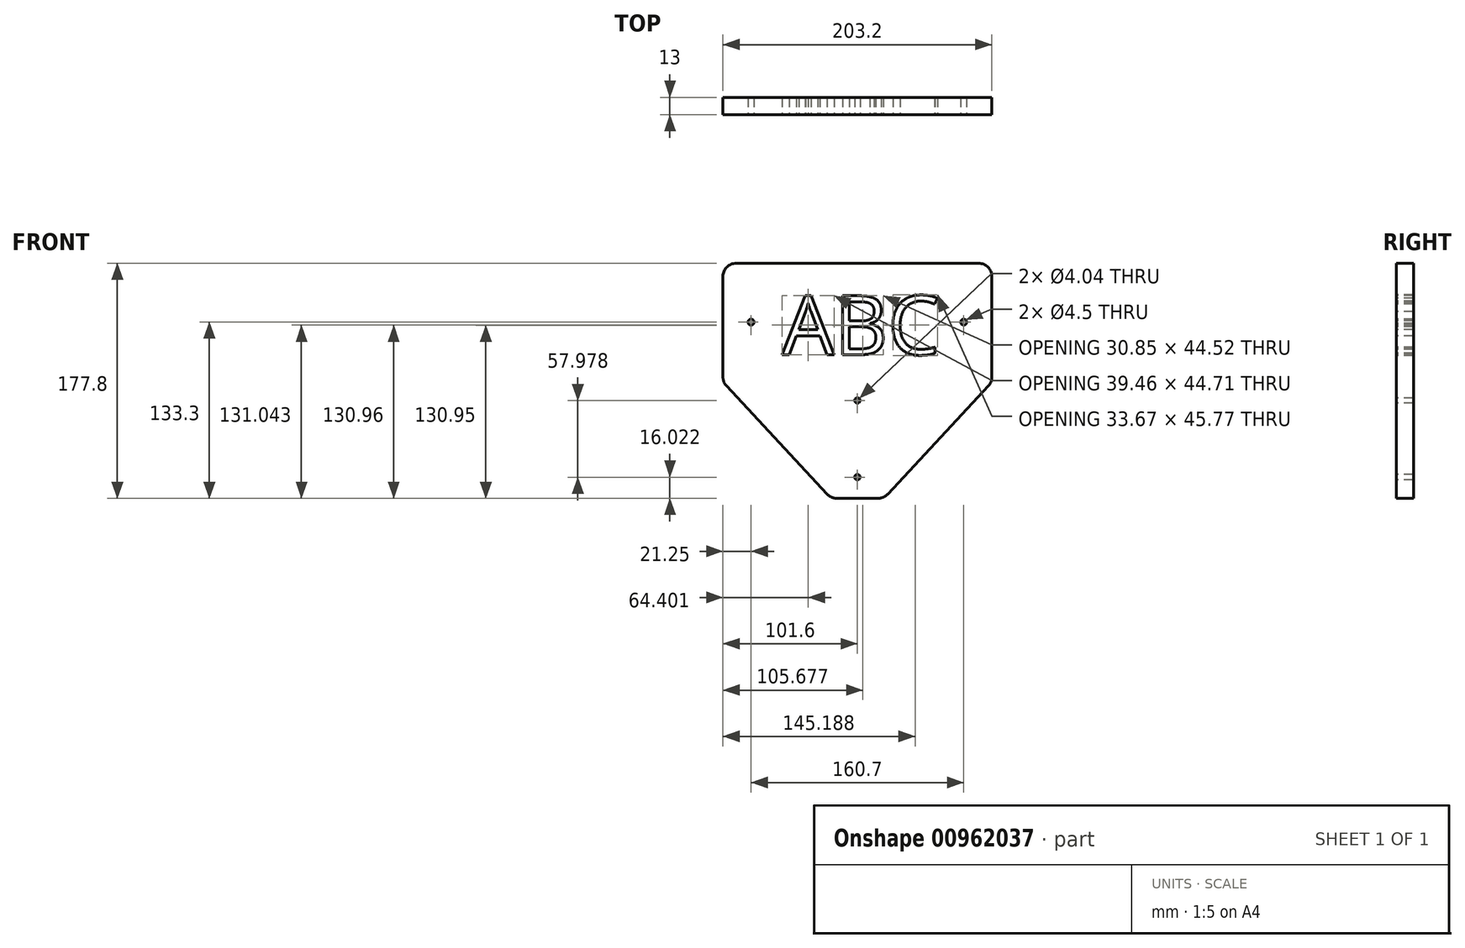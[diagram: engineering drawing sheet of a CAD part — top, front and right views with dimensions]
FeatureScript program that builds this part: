
annotation { "Feature Type Name" : "Feature", "Feature Type Description" : "" }
export const myFeature = defineFeature(function(context is Context, id is Id, definition is map)
    precondition{}
    {
        {
            var Q0;
            Q0=qCreatedBy(makeId("Front.planeOp"),FACE);
            var sketch = newSketch(context, id + "F0", { "sketchPlane" : qUnion([Q0])});
            skLineSegment(sketch, "E0", {"start": v(0, 0) * mm, "end": v(20, 0) * mm});
            skLineSegment(sketch, "E1", {"start": v(20, 0) * mm, "end": v(101.6, 87.8) * mm});
            skLineSegment(sketch, "E2", {"start": v(101.6, 87.8) * mm, "end": v(101.6, 177.8) * mm});
            skLineSegment(sketch, "E3", {"start": v(101.6, 177.8) * mm, "end": v(0, 177.8) * mm});
            skLineSegment(sketch, "E4", {"start": v(0, 177.8) * mm, "end": v(0, 0) * mm, "construction": true});
            skLineSegment(sketch, "E5.MirrorCS", {"start": v(-101.6, 87.8) * mm, "end": v(-101.6, 177.8) * mm});
            skLineSegment(sketch, "E6.MirrorCS", {"start": v(-20, 0) * mm, "end": v(-101.6, 87.8) * mm});
            skLineSegment(sketch, "E7.MirrorCS", {"start": v(0, 0) * mm, "end": v(-20, 0) * mm});
            skLineSegment(sketch, "E8.MirrorCS", {"start": v(-101.6, 177.8) * mm, "end": v(0, 177.8) * mm});
            skSolve(sketch);
        }
        {
            var Q0;
            Q0 = qSketchRegion(id + "F0", true);
            extrude(context, id + "F1", {"entities" : qUnion([Q0]), "depth" : 13 * mm, "offsetDistance" : 25 * mm});
        }
        {
            var Q0;
            Q0=makeQuery(id+"F1.opExtrude","CAP_FACE",FACE,{"disambiguationData":[OSD([sQuery(id+"F0.wireOp",EDGE,"E0"),sQuery(id+"F0.wireOp",EDGE,"E1"),sQuery(id+"F0.wireOp",EDGE,"E2"),sQuery(id+"F0.wireOp",EDGE,"E3"),sQuery(id+"F0.wireOp",EDGE,"E5.MirrorCS"),sQuery(id+"F0.wireOp",EDGE,"E6.MirrorCS"),sQuery(id+"F0.wireOp",EDGE,"E7.MirrorCS"),sQuery(id+"F0.wireOp",EDGE,"E8.MirrorCS")])],"isStart":false});
            var sketch = newSketch(context, id + "F2", { "sketchPlane" : qUnion([Q0])});
            skCircle(sketch, "E9", {"center": v(0, 74) * mm, "radius": 2.02 * mm});
            skCircle(sketch, "E10", {"center": v(0, 16.02) * mm, "radius": 2.02 * mm});
            skCircle(sketch, "E11", {"center": v(-80.35, 133.3) * mm, "radius": 2.25 * mm});
            skCircle(sketch, "E12", {"center": v(80.35, 133.3) * mm, "radius": 2.25 * mm});
            skSolve(sketch);
        }
        {
            var Q0;
            Q0 = qSketchRegion(id + "F2", true);
            extrude(context, id + "F3", {"entities" : qUnion([Q0]), "operationType" : NewBodyOperationType.REMOVE, "oppositeDirection" : true, "depth" : 25 * mm, "offsetDistance" : 25 * mm});
        }
        {
            var Q0;
            Q0=makeQuery(id+"F1.opExtrude","SWEPT_EDGE",EDGE,{"disambiguationData":[OSD([sQuery(id+"F0.wireOp",EDGE,"E2"),sQuery(id+"F0.wireOp",EDGE,"E3")])]});
            var Q1;
            Q1=makeQuery(id+"F1.opExtrude","SWEPT_EDGE",EDGE,{"disambiguationData":[OSD([sQuery(id+"F0.wireOp",EDGE,"E1"),sQuery(id+"F0.wireOp",EDGE,"E2")])]});
            var Q2;
            Q2=makeQuery(id+"F1.opExtrude","SWEPT_EDGE",EDGE,{"disambiguationData":[OSD([sQuery(id+"F0.wireOp",EDGE,"E6.MirrorCS"),sQuery(id+"F0.wireOp",EDGE,"E7.MirrorCS")])]});
            var Q3;
            Q3=makeQuery(id+"F1.opExtrude","SWEPT_EDGE",EDGE,{"disambiguationData":[OSD([sQuery(id+"F0.wireOp",EDGE,"E0"),sQuery(id+"F0.wireOp",EDGE,"E1")])]});
            var Q4;
            Q4=makeQuery(id+"F1.opExtrude","SWEPT_EDGE",EDGE,{"disambiguationData":[OSD([sQuery(id+"F0.wireOp",EDGE,"E5.MirrorCS"),sQuery(id+"F0.wireOp",EDGE,"E6.MirrorCS")])]});
            var Q5;
            Q5=makeQuery(id+"F1.opExtrude","SWEPT_EDGE",EDGE,{"disambiguationData":[OSD([sQuery(id+"F0.wireOp",EDGE,"E5.MirrorCS"),sQuery(id+"F0.wireOp",EDGE,"E8.MirrorCS")])]});
            fillet(context, id + "F4", {"entities" : qUnion([Q0, Q1, Q2, Q3, Q4, Q5]), "radius" : 10 * mm, "tangentPropagation" : true, "allowEdgeOverflow" : false});
        }
        {
            var Q0;
            Q0=makeQuery(id+"F1.opExtrude","CAP_FACE",FACE,{"disambiguationData":[OSD([sQuery(id+"F0.wireOp",EDGE,"E0"),sQuery(id+"F0.wireOp",EDGE,"E1"),sQuery(id+"F0.wireOp",EDGE,"E2"),sQuery(id+"F0.wireOp",EDGE,"E3"),sQuery(id+"F0.wireOp",EDGE,"E5.MirrorCS"),sQuery(id+"F0.wireOp",EDGE,"E6.MirrorCS"),sQuery(id+"F0.wireOp",EDGE,"E7.MirrorCS"),sQuery(id+"F0.wireOp",EDGE,"E8.MirrorCS")])],"isStart":false});
            var sketch = newSketch(context, id + "F5", { "sketchPlane" : qUnion([Q0])});
            skText(sketch, "E13", { "text": "ABC\n", "fontName": "OpenSans-Regular.ttf"});
            const initialGuessF5  = {"E13": [-0.05693, 0.10869, 1, 0, 0.0449]};
            skSetInitialGuess(sketch, initialGuessF5);
            skSolve(sketch);
        }
        {
            var Q0;
            Q0 = qSketchRegion(id + "F5", true);
            extrude(context, id + "F6", {"entities" : qUnion([Q0]), "operationType" : NewBodyOperationType.REMOVE, "oppositeDirection" : true, "depth" : 25 * mm, "offsetDistance" : 25 * mm});
        }
    });
